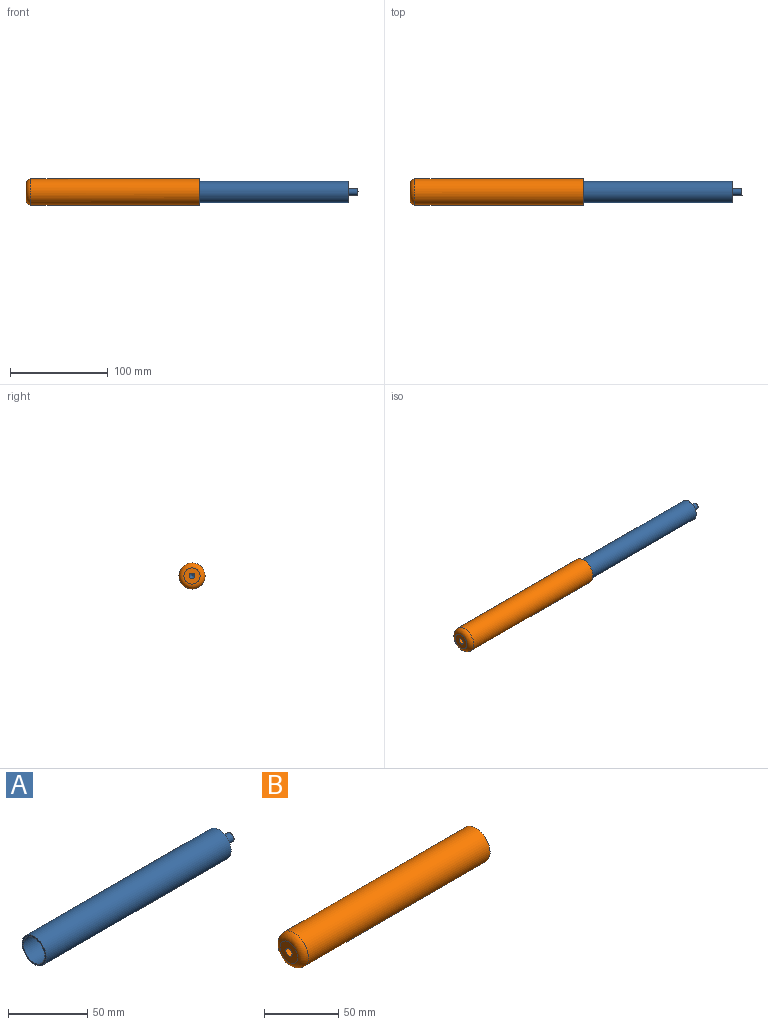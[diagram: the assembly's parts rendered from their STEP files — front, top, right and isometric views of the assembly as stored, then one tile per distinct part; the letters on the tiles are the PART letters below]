
ASSEMBLY  parts=2 mates=1
PART A: 7 faces, bbox 175.3x21.6x21.6 mm
  f0: cylinder r=10.79mm len=165.1mm, axis (-1,0,0), area 11198.2mm2, adj f1,f2
  f1: plane 21.59x21.59mm, normal (1,0,0), area 334.4mm2, adj f0,f5
  f2: plane 21.59x21.59mm, normal (-1,0,0), area 81.1mm2, adj f0,f3
  f3: cylinder r=9.53mm len=152.4mm, axis (-1,0,0), area 9120.7mm2, adj f2,f4
  f4: cone r=0mm half-angle=59deg, axis (-1,0,0), area 332.5mm2, adj f3
  f5: cylinder r=3.17mm len=10.16mm, axis (-1,0,0), area 202.7mm2, adj f1,f6
  f6: plane 6.35x6.35mm, normal (1,0,0), area 31.7mm2, adj f5
PART B: 6 faces, bbox 177.8x28.9x28.9 mm
  f0: cylinder r=13.36mm len=172.72mm, axis (-1,0,0), area 14495.3mm2, adj f1,f5
  f1: plane 26.71x26.71mm, normal (1,0,0), area 150mm2, adj f0,f4
  f2: plane 16.55x16.55mm, normal (-1,0,0), area 187.4mm2, adj f3,f5
  f3: cone r=0mm half-angle=59deg, axis (1,0,0), area 446.4mm2, adj f2,f4
  f4: cylinder r=11.43mm len=172.72mm, axis (1,0,0), area 12404.2mm2, adj f1,f3
  f5: torus R=8.28mm, axis (1,0,0), area 577.1mm2, adj f0,f2
PLACE A t=(108.41,-54.11,44.46)mm
PLACE B rot(axis=(0.08,0.12,0.99),0deg) t=(-56.69,-54.11,44.46)mm
MATE slider A.f0 <-> B.f0  axis (1,0,0) through (273.51,-54.11,44.46)mm
